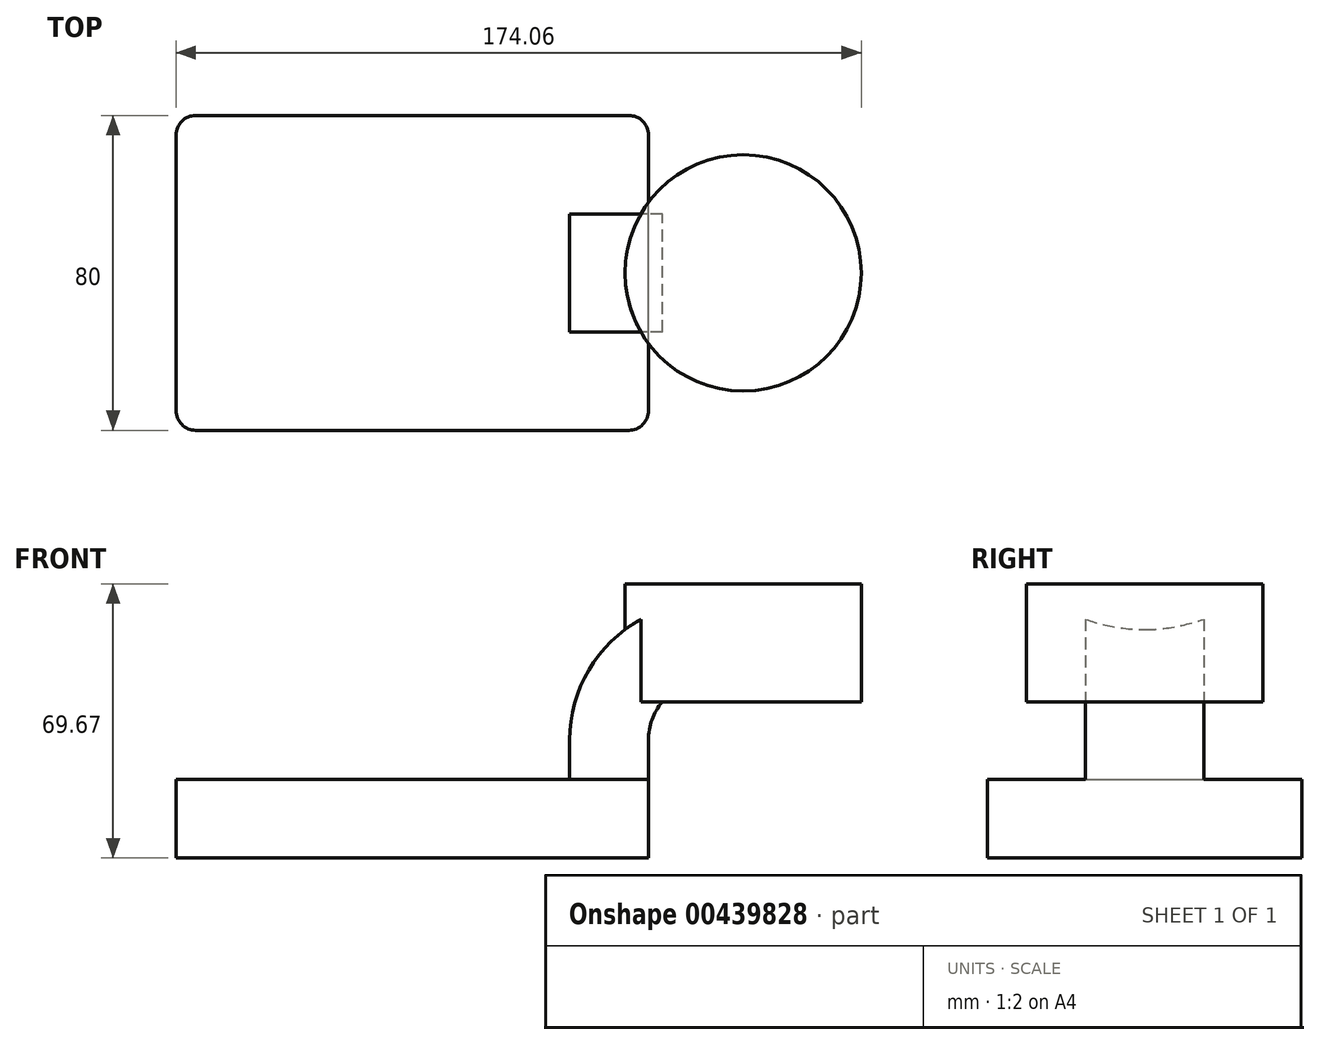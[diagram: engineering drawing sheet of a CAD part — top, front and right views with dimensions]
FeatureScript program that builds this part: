
annotation { "Feature Type Name" : "Feature", "Feature Type Description" : "" }
export const myFeature = defineFeature(function(context is Context, id is Id, definition is map)
    precondition{}
    {
        {
            var Q0;
            Q0=qCreatedBy(makeId("Front.planeOp"),FACE);
            var sketch = newSketch(context, id + "F0", { "sketchPlane" : qUnion([Q0])});
            skLineSegment(sketch, "E0.bottom", {"start": v(60, -10) * mm, "end": v(-60, -10) * mm});
            skLineSegment(sketch, "E0.top", {"start": v(60, 10) * mm, "end": v(-60, 10) * mm});
            skLineSegment(sketch, "E0.left", {"start": v(60, -10) * mm, "end": v(60, 10) * mm});
            skLineSegment(sketch, "E0.right", {"start": v(-60, -10) * mm, "end": v(-60, 10) * mm});
            skPoint(sketch, "E0.middle", {"position": v(0, 0) * mm});
            skLineSegment(sketch, "E1.bottom", {"start": v(114.06, 29.67) * mm, "end": v(84.06, 29.67) * mm});
            skLineSegment(sketch, "E1.top", {"start": v(114.06, 59.67) * mm, "end": v(84.06, 59.67) * mm});
            skLineSegment(sketch, "E1.left", {"start": v(114.06, 29.67) * mm, "end": v(114.06, 59.67) * mm});
            skLineSegment(sketch, "E1.right", {"start": v(84.06, 29.67) * mm, "end": v(84.06, 59.67) * mm});
            skPoint(sketch, "E1.middle", {"position": v(99.06, 44.67) * mm});
            skLineSegment(sketch, "E2", {"start": v(60, 10) * mm, "end": v(60, 20) * mm});
            skArc(sketch, "E3", {"start": v(60, 20) * mm, "mid": v(64.4, 30.6) * mm, "end": v(75, 35) * mm});
            skLineSegment(sketch, "E4", {"start": v(75, 35) * mm, "end": v(95, 35) * mm});
            skLineSegment(sketch, "E5.0", {"start": v(75, 55) * mm, "end": v(95.26, 55) * mm});
            skArc(sketch, "E5.1", {"start": v(40, 20) * mm, "mid": v(50.25, 44.75) * mm, "end": v(75, 55) * mm});
            skLineSegment(sketch, "E5.2", {"start": v(40, 10) * mm, "end": v(40, 20) * mm});
            skFitSpline(sketch, "E6", {"points": [v(-60, 10) * mm, v(75, 55) * mm], "startDerivative": vector(13.42, 125.17) * mm, "endDerivative": vector(203.7, -0.32) * mm});
            skSolve(sketch);
        }
        {
            var Q0;
            Q0=makeQuery(id+"F0.imprint","IMPRINT",FACE,{"disambiguationData":[TD([[makeQuery(id+"F0.imprint","IMPRINT",EDGE,{"derivedFrom":sQuery(id+"F0.wireOp",EDGE,"E0.bottom")}),-1.0]])]});
            extrude(context, id + "F1", {"entities" : qUnion([Q0]), "endBound" : BoundingType.SYMMETRIC, "depth" : 80 * mm});
        }
        {
            var Q0;
            {var subQ1=sQuery(id+"F0.wireOp",EDGE,"E2");Q0=makeQuery(id+"F0.imprint","IMPRINT",FACE,{"disambiguationData":[TD([[makeQuery(id+"F0.imprint","IMPRINT",EDGE,{"derivedFrom":subQ1}),1.0]])]});}
            extrude(context, id + "F2", {"entities" : qUnion([Q0]), "operationType" : NewBodyOperationType.ADD, "endBound" : BoundingType.SYMMETRIC, "depth" : 30 * mm});
        }
        {
            var Q0;
            Q0=makeQuery(id+"F0.imprint","IMPRINT",FACE,{"disambiguationData":[TD([[makeQuery(id+"F0.imprint","IMPRINT",EDGE,{"derivedFrom":sQuery(id+"F0.wireOp",EDGE,"E5.1")}),1.0]])]});
            extrude(context, id + "F3", {"entities" : qUnion([Q0]), "operationType" : NewBodyOperationType.ADD, "endBound" : BoundingType.SYMMETRIC, "depth" : 10 * mm});
        }
        {
            var Q0;
            {var subQ1=sQuery(id+"F0.wireOp",EDGE,"E1.bottom");Q0=makeQuery(id+"F0.imprint","IMPRINT",FACE,{"disambiguationData":[TD([[makeQuery(id+"F0.imprint","IMPRINT",EDGE,{"derivedFrom":subQ1}),-1.0]])]});}
            var Q1;
            Q1=sQuery(id+"F0.wireOp",EDGE,"E1.right");
            revolve(context, id + "F4", {"operationType" : NewBodyOperationType.ADD, "entities" : qUnion([Q0]), "axis" : qUnion([Q1]), "revolveType" : RevolveType.FULL});
        }
        {
            var Q0;
            Q0=makeQuery(id+"F1.opExtrude","CAP_EDGE",EDGE,{"disambiguationData":[OSD([sQuery(id+"F0.wireOp",EDGE,"E0.right")])],"isStart":false});
            var Q1;
            Q1=makeQuery(id+"F1.opExtrude","CAP_EDGE",EDGE,{"disambiguationData":[OSD([sQuery(id+"F0.wireOp",EDGE,"E0.left")])],"isStart":false});
            var Q2;
            Q2=makeQuery(id+"F1.opExtrude","CAP_EDGE",EDGE,{"disambiguationData":[OSD([sQuery(id+"F0.wireOp",EDGE,"E0.left")])],"isStart":true});
            var Q3;
            Q3=makeQuery(id+"F1.opExtrude","CAP_EDGE",EDGE,{"disambiguationData":[OSD([sQuery(id+"F0.wireOp",EDGE,"E0.right")])],"isStart":true});
            fillet(context, id + "F5", {"entities" : qUnion([Q0, Q1, Q2, Q3]), "radius" : 5 * mm, "tangentPropagation" : true, "allowEdgeOverflow" : false});
        }
    });
